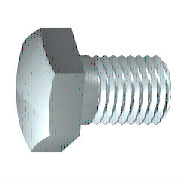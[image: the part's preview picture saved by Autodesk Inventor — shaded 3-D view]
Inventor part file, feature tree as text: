
AUTODESK INVENTOR PART (.ipt)
format: ipt  version: 2020 (Build 240168000, 168)  size: 196,608 bytes
history: native  units: mm (DEFAULTED — no unit token found)
features: sketch x3, extrude x1, chamfer x1, plane x1
ambient origin geometry x7: Origin, YZ Plane, XZ Plane, X Axis, Y Axis, Z Axis, Center Point
bodies: Solid1 (feature_tree), Body (feature_tree)
feature tree (6):
  extrude  "Head"  Depth=22.6mm
  chamfer  "Chamfer1"  Distance=3.0mm
  plane  "Work Plane1"
  sketch  "Sketch1"  dims[d0=25.0mm d1=22.6mm]
  sketch  "Sketch2"  dims[d2=5.0mm]
  sketch  "Sketch4"  dims[d12=90.0deg d3=3.0mm d4=0.0mm d5=30.0deg d21=90.0deg d6=0.49076mm d7=0.49086mm d8=0.0mm d9=0.5001mm d10=6.7mm d11=8.0mm d13=0.49086mm d14=4.566987mm d15=22.6mm d16=0.0mm d19=8.0mm d55=45.0deg d57=0.0mm d58=0.0mm]
